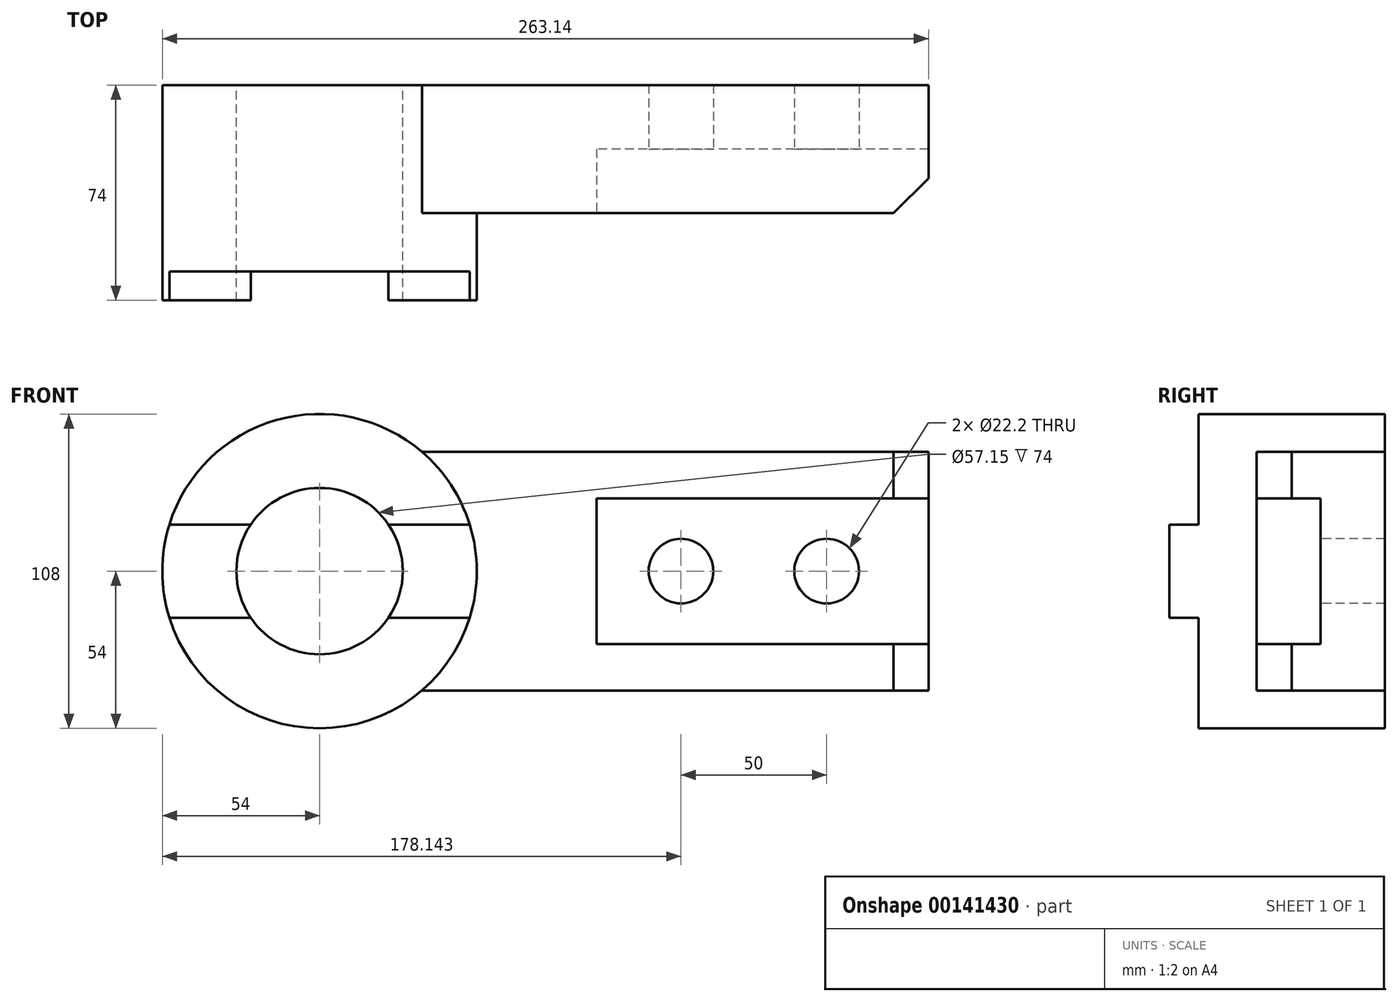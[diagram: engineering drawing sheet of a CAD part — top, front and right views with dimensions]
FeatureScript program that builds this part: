
annotation { "Feature Type Name" : "Feature", "Feature Type Description" : "" }
export const myFeature = defineFeature(function(context is Context, id is Id, definition is map)
    precondition{}
    {
        {
            var Q0;
            Q0=qCreatedBy(makeId("Front.planeOp"),FACE);
            var sketch = newSketch(context, id + "F0", { "sketchPlane" : qUnion([Q0])});
            skCircle(sketch, "E0", {"center": v(0, 0) * mm, "radius": 28.57 * mm});
            skCircle(sketch, "E1", {"center": v(0, 0) * mm, "radius": 54 * mm});
            skLineSegment(sketch, "E2", {"start": v(-84.95, 0) * mm, "end": v(255.36, 0) * mm, "construction": true});
            skLineSegment(sketch, "E3", {"start": v(35.14, 41) * mm, "end": v(209.14, 41) * mm});
            skLineSegment(sketch, "E4", {"start": v(209.14, 41) * mm, "end": v(209.14, -41) * mm});
            skLineSegment(sketch, "E5", {"start": v(209.14, -41) * mm, "end": v(35.14, -41) * mm});
            skSolve(sketch);
        }
        {
            var Q0;
            Q0=makeQuery(id+"F0.imprint","IMPRINT",FACE,{"disambiguationData":[TD([[makeQuery(id+"F0.imprint","IMPRINT",EDGE,{"derivedFrom":sQuery(id+"F0.wireOp",EDGE,"E0")}),-1.0]])]});
            extrude(context, id + "F1", {"entities" : qUnion([Q0]), "depth" : 64 * mm});
        }
        {
            var Q0;
            {var subQ0=sQuery(id+"F0.wireOp",EDGE,"E3");Q0=makeQuery(id+"F0.imprint","IMPRINT",FACE,{"disambiguationData":[TD([[makeQuery(id+"F0.imprint","IMPRINT",EDGE,{"derivedFrom":subQ0}),-1.0]])]});}
            extrude(context, id + "F2", {"entities" : qUnion([Q0]), "operationType" : NewBodyOperationType.ADD, "depth" : 44 * mm});
        }
        {
            var Q0;
            Q0=makeQuery(id+"F2.opExtrude","SWEPT_FACE",FACE,{"disambiguationData":[OSD([sQuery(id+"F0.wireOp",EDGE,"E3")])]});
            var sketch = newSketch(context, id + "F3", { "sketchPlane" : qUnion([Q0])});
            skLineSegment(sketch, "E6", {"start": v(197.14, -44) * mm, "end": v(209.14, -32) * mm});
            skLineSegment(sketch, "E7", {"start": v(209.14, -32) * mm, "end": v(209.14, -44) * mm});
            skLineSegment(sketch, "E8", {"start": v(209.14, -44) * mm, "end": v(197.14, -44) * mm});
            skSolve(sketch);
        }
        {
            var Q0;
            Q0=makeQuery(id+"F2.opExtrude","CAP_FACE",FACE,{"disambiguationData":[OSD([sQuery(id+"F0.wireOp",EDGE,"E1"),sQuery(id+"F0.wireOp",EDGE,"E3"),sQuery(id+"F0.wireOp",EDGE,"E4"),sQuery(id+"F0.wireOp",EDGE,"E5")])],"isStart":false});
            var sketch = newSketch(context, id + "F4", { "sketchPlane" : qUnion([Q0])});
            skLineSegment(sketch, "E9", {"start": v(209.14, 25) * mm, "end": v(95.14, 25) * mm});
            skLineSegment(sketch, "E10", {"start": v(95.14, 25) * mm, "end": v(95.14, -25) * mm});
            skLineSegment(sketch, "E11", {"start": v(95.14, -25) * mm, "end": v(209.14, -25) * mm});
            skLineSegment(sketch, "E12", {"start": v(209.14, -25) * mm, "end": v(209.14, 25) * mm});
            skSolve(sketch);
        }
        {
            var Q0;
            Q0 = qSketchRegion(id + "F4", true);
            extrude(context, id + "F5", {"entities" : qUnion([Q0]), "operationType" : NewBodyOperationType.REMOVE, "oppositeDirection" : true, "depth" : 22 * mm});
        }
        {
            var Q0;
            Q0 = qSketchRegion(id + "F3", true);
            extrude(context, id + "F6", {"entities" : qUnion([Q0]), "operationType" : NewBodyOperationType.REMOVE, "endBound" : BoundingType.THROUGH_ALL, "oppositeDirection" : true, "depth" : 25 * mm, "hasSecondDirection" : true, "secondDirectionOppositeDirection" : false, "secondDirectionDepth" : 25 * mm});
        }
        {
            var Q0;
            Q0=makeQuery(id+"F5.boolean.opBoolean","COPY",FACE,{"derivedFrom":makeQuery(id+"F5.opExtrude","CAP_FACE",FACE,{"disambiguationData":[OSD([sQuery(id+"F4.wireOp",EDGE,"E9"),sQuery(id+"F4.wireOp",EDGE,"E10"),sQuery(id+"F4.wireOp",EDGE,"E11"),sQuery(id+"F4.wireOp",EDGE,"E12")])],"isStart":false})});
            var sketch = newSketch(context, id + "F7", { "sketchPlane" : qUnion([Q0])});
            skCircle(sketch, "E13", {"center": v(124.14, 0) * mm, "radius": 11.1 * mm});
            skCircle(sketch, "E14", {"center": v(174.14, 0) * mm, "radius": 11.1 * mm});
            skSolve(sketch);
        }
        {
            var Q0;
            Q0 = qSketchRegion(id + "F7", true);
            extrude(context, id + "F8", {"entities" : qUnion([Q0]), "operationType" : NewBodyOperationType.REMOVE, "endBound" : BoundingType.THROUGH_ALL, "oppositeDirection" : true, "depth" : 25 * mm});
        }
        {
            var Q0;
            Q0=makeQuery(id+"F1.opExtrude","CAP_FACE",FACE,{"disambiguationData":[OSD([sQuery(id+"F0.wireOp",EDGE,"E0"),sQuery(id+"F0.wireOp",EDGE,"E1")])],"isStart":false});
            var sketch = newSketch(context, id + "F9", { "sketchPlane" : qUnion([Q0])});
            skArc(sketch, "E15", {"start": v(-23.68, 16) * mm, "mid": v(-28.58, 0) * mm, "end": v(-23.68, -16) * mm});
            skArc(sketch, "E16", {"start": v(-51.58, 16) * mm, "mid": v(-54, 0) * mm, "end": v(-51.58, -16) * mm});
            skLineSegment(sketch, "E17", {"start": v(-51.58, 16) * mm, "end": v(-23.68, 16) * mm});
            skLineSegment(sketch, "E18", {"start": v(-51.58, -16) * mm, "end": v(-23.68, -16) * mm});
            skSolve(sketch);
        }
        {
            var Q0;
            Q0 = qSketchRegion(id + "F9", true);
            extrude(context, id + "F10", {"entities" : qUnion([Q0]), "operationType" : NewBodyOperationType.ADD, "depth" : 10 * mm});
        }
        {
            var Q0;
            Q0=makeQuery(id+"F1.opExtrude","CAP_FACE",FACE,{"disambiguationData":[OSD([sQuery(id+"F0.wireOp",EDGE,"E0"),sQuery(id+"F0.wireOp",EDGE,"E1")])],"isStart":false});
            var sketch = newSketch(context, id + "F11", { "sketchPlane" : qUnion([Q0])});
            skArc(sketch, "E19", {"start": v(23.68, -16) * mm, "mid": v(28.57, 0) * mm, "end": v(23.68, 16) * mm});
            skArc(sketch, "E20", {"start": v(51.58, -16) * mm, "mid": v(54, 0) * mm, "end": v(51.58, 16) * mm});
            skLineSegment(sketch, "E21", {"start": v(23.68, 16) * mm, "end": v(51.58, 16) * mm});
            skLineSegment(sketch, "E22", {"start": v(23.68, -16) * mm, "end": v(51.58, -16) * mm});
            skSolve(sketch);
        }
        {
            var Q0;
            Q0 = qSketchRegion(id + "F11", true);
            extrude(context, id + "F12", {"entities" : qUnion([Q0]), "operationType" : NewBodyOperationType.ADD, "depth" : 10 * mm});
        }
    });
